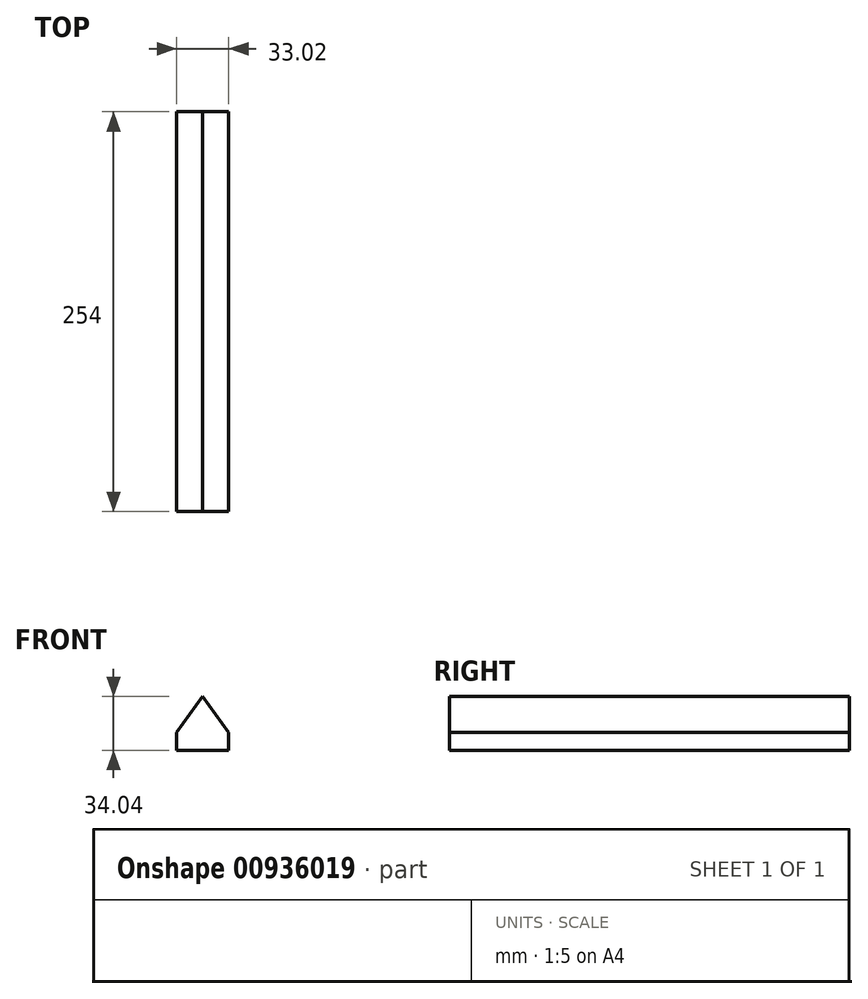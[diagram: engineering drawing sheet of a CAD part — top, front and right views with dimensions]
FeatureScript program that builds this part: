
annotation { "Feature Type Name" : "Feature", "Feature Type Description" : "" }
export const myFeature = defineFeature(function(context is Context, id is Id, definition is map)
    precondition{}
    {
        {
            var Q0;
            Q0=qCreatedBy(makeId("Front.planeOp"),FACE);
            var sketch = newSketch(context, id + "F0", { "sketchPlane" : qUnion([Q0])});
            skLineSegment(sketch, "E0.bottom", {"start": v(0, 0) * mm, "end": v(33.02, 0) * mm});
            skLineSegment(sketch, "E0.top", {"start": v(0, 11.43) * mm, "end": v(33.02, 11.43) * mm, "construction": true});
            skLineSegment(sketch, "E0.left", {"start": v(0, 0) * mm, "end": v(0, 11.43) * mm});
            skLineSegment(sketch, "E0.right", {"start": v(33.02, 0) * mm, "end": v(33.02, 11.43) * mm});
            skLineSegment(sketch, "E1", {"start": v(16.51, 11.43) * mm, "end": v(16.51, 34.04) * mm, "construction": true});
            skLineSegment(sketch, "E2", {"start": v(16.51, 34.04) * mm, "end": v(0, 11.43) * mm});
            skLineSegment(sketch, "E3", {"start": v(16.5, 34.04) * mm, "end": v(33.02, 11.43) * mm});
            skLineSegment(sketch, "E4", {"start": v(0, 0) * mm, "end": v(0, 33.72) * mm, "construction": true});
            skSolve(sketch);
        }
        {
            var Q0;
            Q0 = qSketchRegion(id + "F0", true);
            extrude(context, id + "F1", {"entities" : qUnion([Q0]), "depth" : 254 * mm, "offsetDistance" : 25.4 * mm});
        }
    });
